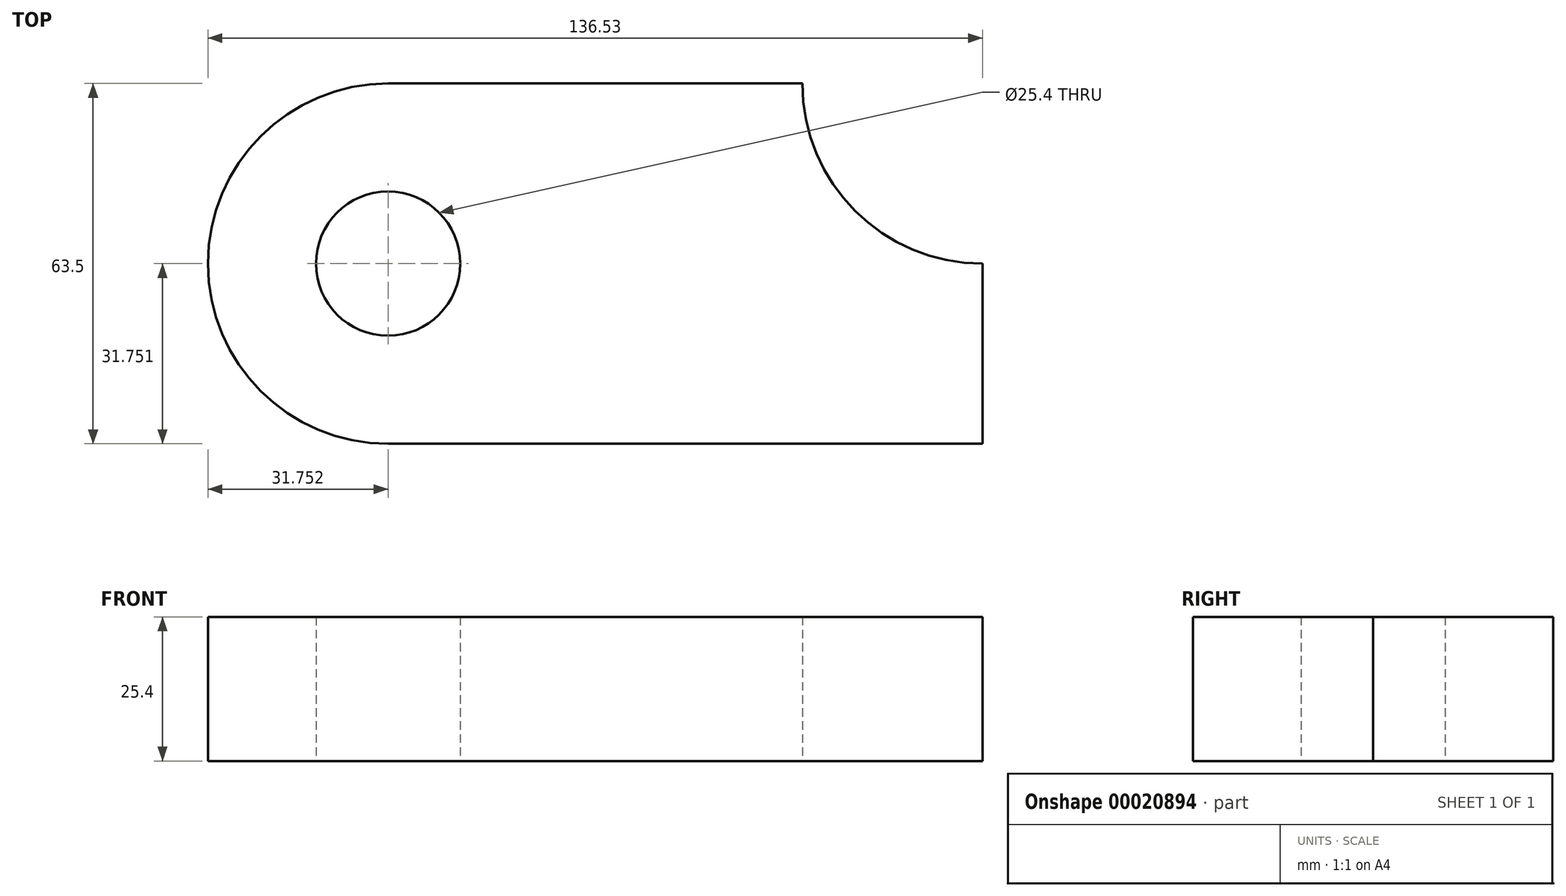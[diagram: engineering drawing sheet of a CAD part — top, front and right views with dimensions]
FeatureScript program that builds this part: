
annotation { "Feature Type Name" : "Feature", "Feature Type Description" : "" }
export const myFeature = defineFeature(function(context is Context, id is Id, definition is map)
    precondition{}
    {
        {
            var Q0;
            Q0=qCreatedBy(makeId("Top.planeOp"),FACE);
            var sketch = newSketch(context, id + "F0", { "sketchPlane" : qUnion([Q0])});
            skLineSegment(sketch, "E0.bottom", {"start": v(-56.7, 34.66) * mm, "end": v(16.32, 34.66) * mm});
            skLineSegment(sketch, "E0.top", {"start": v(-56.7, -28.84) * mm, "end": v(48.07, -28.84) * mm});
            skLineSegment(sketch, "E0.right", {"start": v(48.07, 2.91) * mm, "end": v(48.07, -28.84) * mm});
            skArc(sketch, "E1", {"start": v(-56.7, 34.66) * mm, "mid": v(-88.46, 2.91) * mm, "end": v(-56.7, -28.84) * mm});
            skCircle(sketch, "E2", {"center": v(-56.7, 2.91) * mm, "radius": 12.7 * mm});
            skArc(sketch, "E3", {"start": v(16.32, 34.66) * mm, "mid": v(25.62, 12.21) * mm, "end": v(48.07, 2.91) * mm});
            skSolve(sketch);
        }
        {
            var Q0;
            Q0=makeQuery(id+"F0.imprint","IMPRINT",FACE,{"disambiguationData":[TD([[makeQuery(id+"F0.imprint","IMPRINT",EDGE,{"derivedFrom":sQuery(id+"F0.wireOp",EDGE,"E0.bottom")}),-1.0]])]});
            extrude(context, id + "F1", {"entities" : qUnion([Q0]), "depth" : 25.4 * mm});
        }
    });
